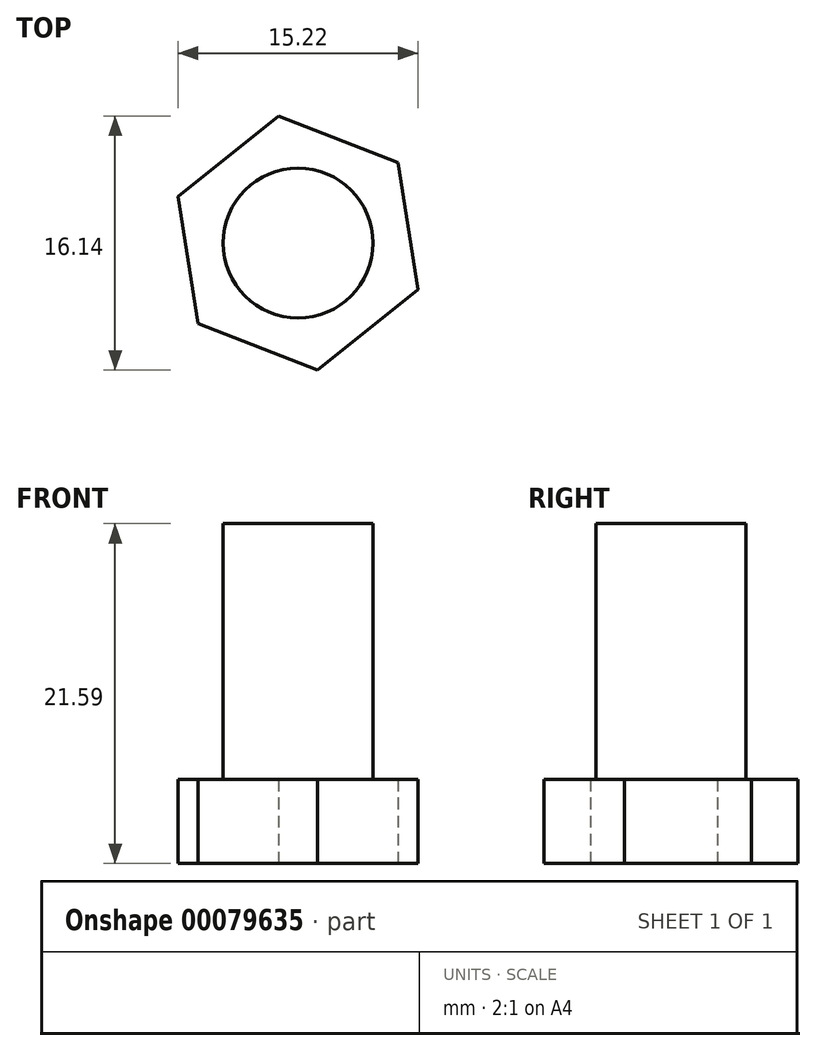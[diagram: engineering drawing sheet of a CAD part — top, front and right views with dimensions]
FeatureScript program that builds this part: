
annotation { "Feature Type Name" : "Feature", "Feature Type Description" : "" }
export const myFeature = defineFeature(function(context is Context, id is Id, definition is map)
    precondition{}
    {
        {
            var Q0;
            Q0=qCreatedBy(makeId("Top.planeOp"),FACE);
            var sketch = newSketch(context, id + "F0", { "sketchPlane" : qUnion([Q0])});
            skCircle(sketch, "E0.cCircle", {"center": v(0, 0) * mm, "radius": 7.07 * mm, "construction": true});
            skLineSegment(sketch, "E0.0", {"start": v(-7.6, 2.95) * mm, "end": v(-1.25, 8.07) * mm});
            skLineSegment(sketch, "E0.1", {"start": v(-1.25, 8.07) * mm, "end": v(6.36, 5.11) * mm});
            skLineSegment(sketch, "E0.2", {"start": v(6.36, 5.11) * mm, "end": v(7.6, -2.95) * mm});
            skLineSegment(sketch, "E0.3", {"start": v(7.6, -2.95) * mm, "end": v(1.25, -8.07) * mm});
            skLineSegment(sketch, "E0.4", {"start": v(1.25, -8.07) * mm, "end": v(-6.36, -5.11) * mm});
            skLineSegment(sketch, "E0.5", {"start": v(-6.36, -5.11) * mm, "end": v(-7.6, 2.95) * mm});
            skPoint(sketch, "E0.0.midPoint", {"position": v(-4.43, 5.5) * mm});
            skSolve(sketch);
        }
        {
            var Q0;
            Q0=makeQuery(id+"F0.imprint","IMPRINT",FACE,{"disambiguationData":[TD([[makeQuery(id+"F0.imprint","IMPRINT",EDGE,{"derivedFrom":sQuery(id+"F0.wireOp",EDGE,"E0.0")}),-1.0]])]});
            extrude(context, id + "F1", {"entities" : qUnion([Q0]), "endBound" : BoundingType.SYMMETRIC, "depth" : 5.33 * mm});
        }
        {
            var Q0;
            Q0=makeQuery(id+"F1.opExtrude","CAP_FACE",FACE,{"disambiguationData":[OSD([sQuery(id+"F0.wireOp",EDGE,"E0.0"),sQuery(id+"F0.wireOp",EDGE,"E0.1"),sQuery(id+"F0.wireOp",EDGE,"E0.2"),sQuery(id+"F0.wireOp",EDGE,"E0.3"),sQuery(id+"F0.wireOp",EDGE,"E0.4"),sQuery(id+"F0.wireOp",EDGE,"E0.5")])],"isStart":false});
            var sketch = newSketch(context, id + "F2", { "sketchPlane" : qUnion([Q0])});
            skCircle(sketch, "E1", {"center": v(0, 0) * mm, "radius": 4.76 * mm});
            skSolve(sketch);
        }
        {
            var Q0;
            Q0=makeQuery(id+"F2.imprint","IMPRINT",FACE,{"disambiguationData":[TD([[makeQuery(id+"F2.imprint","IMPRINT",EDGE,{"derivedFrom":sQuery(id+"F2.wireOp",EDGE,"E1")}),1.0]])]});
            extrude(context, id + "F3", {"entities" : qUnion([Q0]), "operationType" : NewBodyOperationType.ADD, "depth" : 16.26 * mm});
        }
    });
